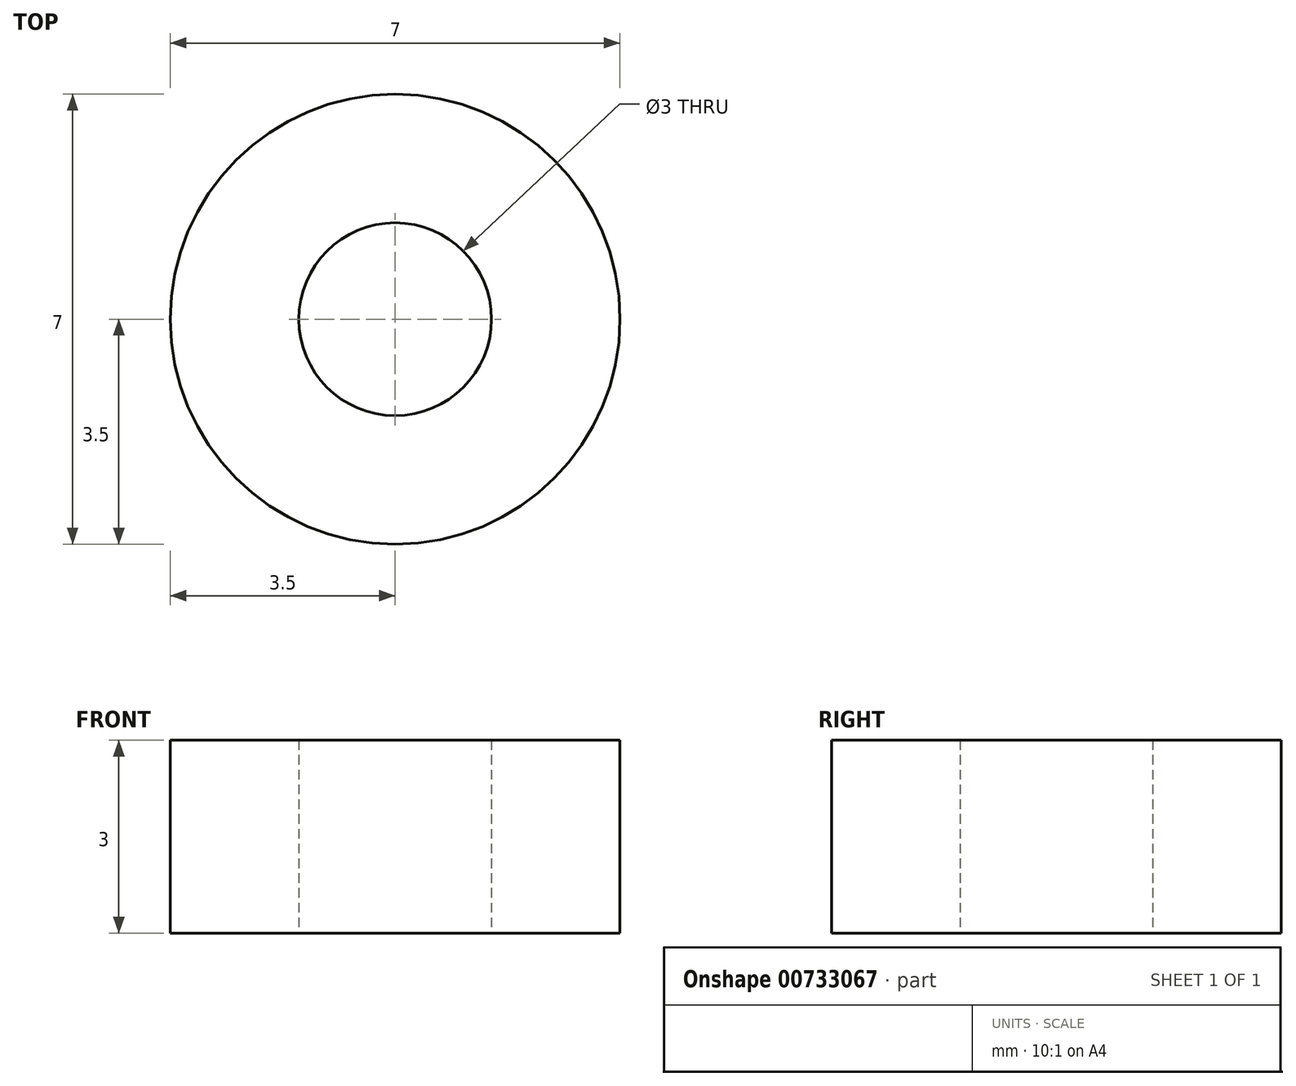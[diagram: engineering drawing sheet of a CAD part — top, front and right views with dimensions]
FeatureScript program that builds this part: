
annotation { "Feature Type Name" : "Feature", "Feature Type Description" : "" }
export const myFeature = defineFeature(function(context is Context, id is Id, definition is map)
    precondition{}
    {
        {
            var Q0;
            Q0=qCreatedBy(makeId("Top.planeOp"),FACE);
            var sketch = newSketch(context, id + "F0", { "sketchPlane" : qUnion([Q0])});
            skCircle(sketch, "E0", {"center": v(0, 0) * mm, "radius": 3.5 * mm});
            skCircle(sketch, "E1", {"center": v(0, 0) * mm, "radius": 1.5 * mm});
            skSolve(sketch);
        }
        {
            var Q0;
            Q0=qSketchRegion(id+"F0",true);
            extrude(context, id + "F1", {"entities" : qUnion([Q0]), "depth" : 3 * mm, "offsetDistance" : 25 * mm});
        }
    });
